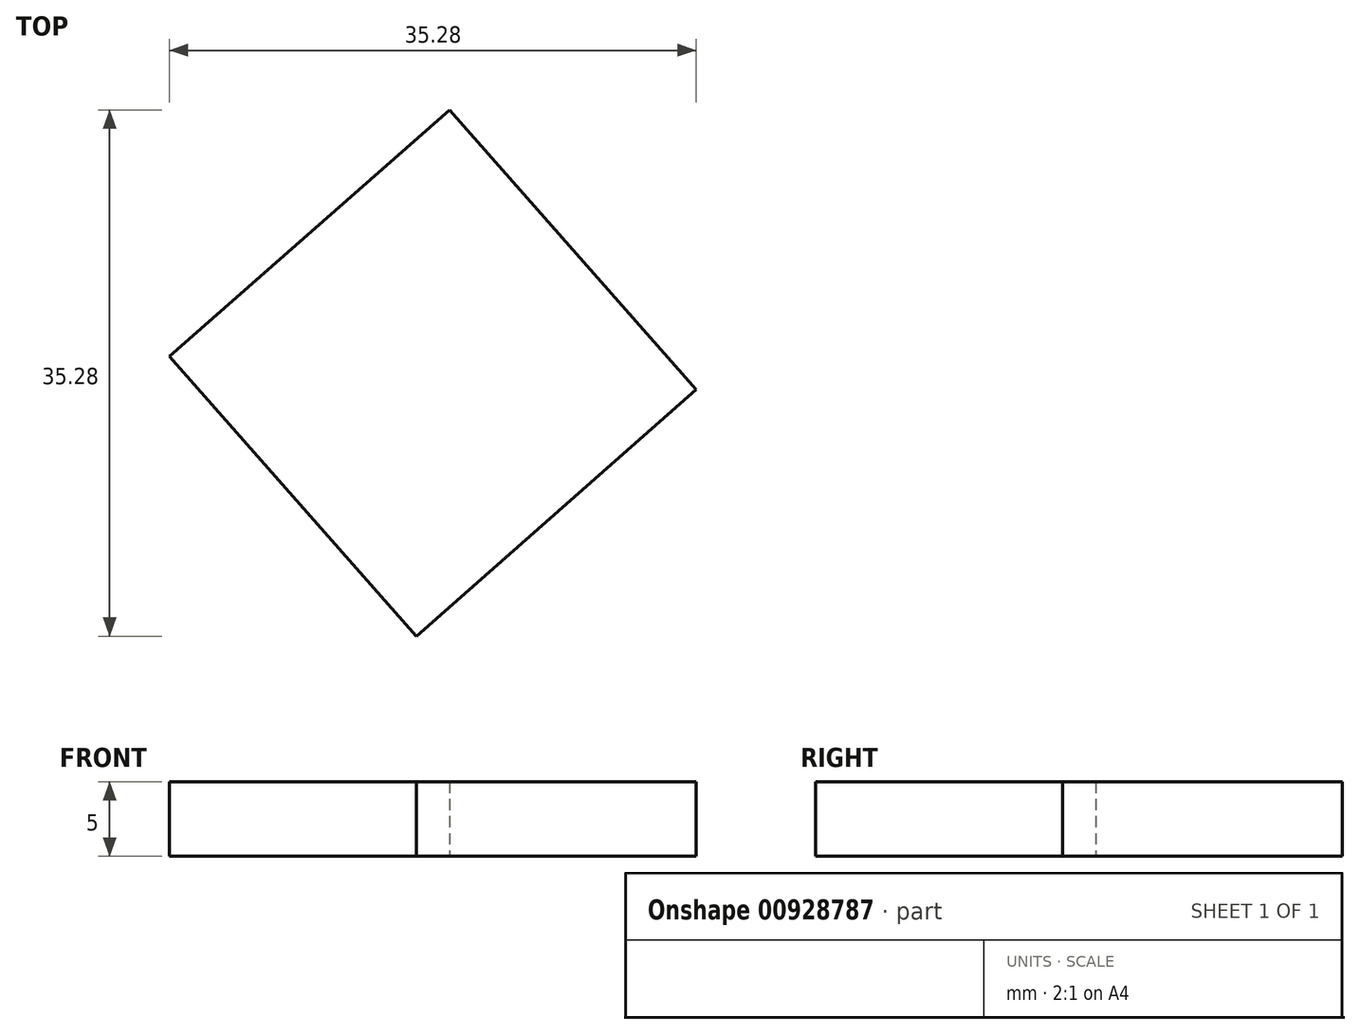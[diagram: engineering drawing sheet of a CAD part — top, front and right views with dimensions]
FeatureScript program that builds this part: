
annotation { "Feature Type Name" : "Feature", "Feature Type Description" : "" }
export const myFeature = defineFeature(function(context is Context, id is Id, definition is map)
    precondition{}
    {
        {
            var Q0;
            Q0=qCreatedBy(makeId("Top.planeOp"),FACE);
            var sketch = newSketch(context, id + "F0", { "sketchPlane" : qUnion([Q0])});
            skCircle(sketch, "E0.cCircle", {"center": v(0, 0) * mm, "radius": 12.5 * mm, "construction": true});
            skLineSegment(sketch, "E0.0", {"start": v(17.64, -1.12) * mm, "end": v(-1.12, -17.64) * mm});
            skLineSegment(sketch, "E0.1", {"start": v(-1.12, -17.64) * mm, "end": v(-17.64, 1.12) * mm});
            skLineSegment(sketch, "E0.2", {"start": v(-17.64, 1.12) * mm, "end": v(1.12, 17.64) * mm});
            skLineSegment(sketch, "E0.3", {"start": v(1.12, 17.64) * mm, "end": v(17.64, -1.12) * mm});
            skPoint(sketch, "E0.0.midPoint", {"position": v(8.26, -9.38) * mm});
            skSolve(sketch);
        }
        {
            var Q0;
            Q0=makeQuery(id+"F0.imprint","IMPRINT",FACE,{"disambiguationData":[TD([[makeQuery(id+"F0.imprint","IMPRINT",EDGE,{"derivedFrom":sQuery(id+"F0.wireOp",EDGE,"E0.0")}),-1.0]])]});
            extrude(context, id + "F1", {"entities" : qUnion([Q0]), "depth" : 5 * mm, "offsetDistance" : 25 * mm});
        }
    });
